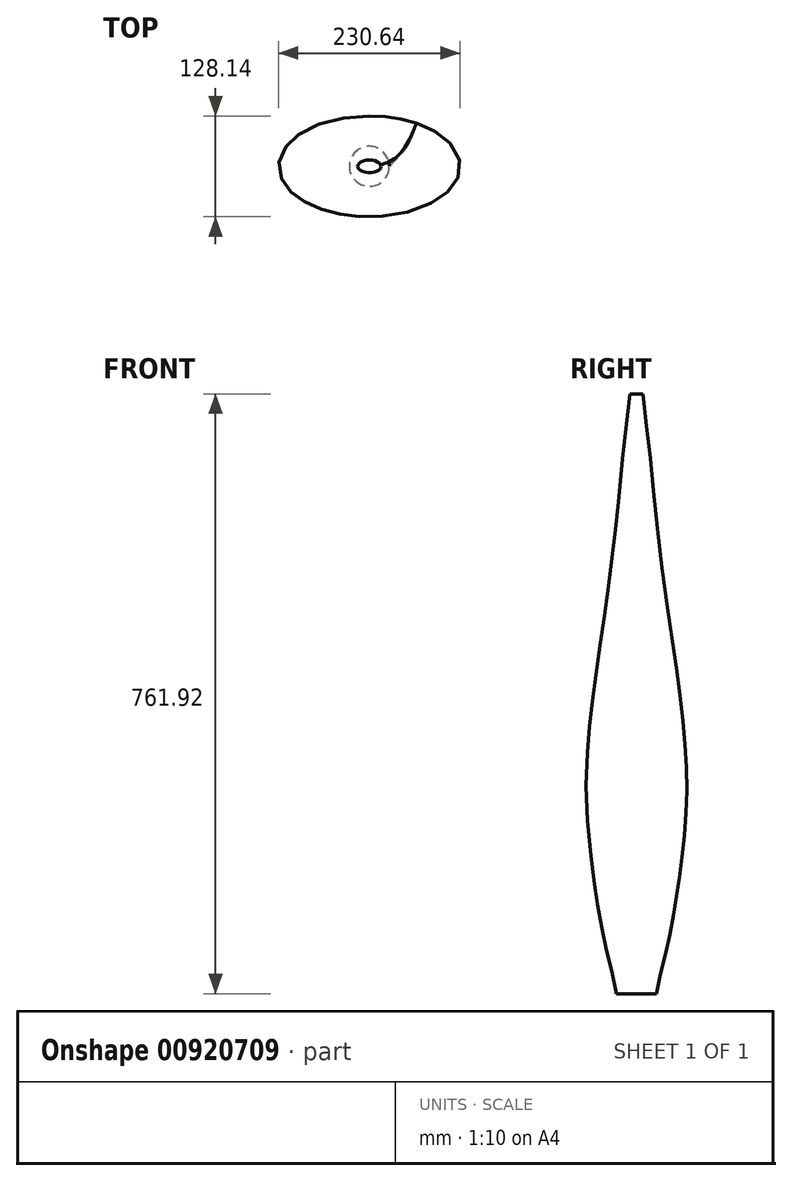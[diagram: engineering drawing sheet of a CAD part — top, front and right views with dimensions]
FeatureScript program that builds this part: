
annotation { "Feature Type Name" : "Feature", "Feature Type Description" : "" }
export const myFeature = defineFeature(function(context is Context, id is Id, definition is map)
    precondition{}
    {
        {
            var Q0;
            Q0=qCreatedBy(makeId("Top.planeOp"),FACE);
            var sketch = newSketch(context, id + "F0", { "sketchPlane" : qUnion([Q0])});
            skEllipse(sketch, "E0", {"center": v(0, 0) * mm, "majorRadius": 25.4 * mm, "minorRadius": 25.4 * mm, "majorAxis": v(1, 0)});
            skSolve(sketch);
        }
        {
            var Q0;
            Q0=qCreatedBy(makeId("Front.planeOp"),FACE);
            var sketch = newSketch(context, id + "F1", { "sketchPlane" : qUnion([Q0])});
            skLineSegment(sketch, "E1", {"start": v(0, 0) * mm, "end": v(0, 84.66) * mm, "construction": true});
            skPoint(sketch, "E2", {"position": v(0, 84.66) * mm});
            skPoint(sketch, "E3.0.1.0", {"position": v(0, 169.32) * mm});
            skPoint(sketch, "E3.0.2.0", {"position": v(0, 253.97) * mm});
            skPoint(sketch, "E3.0.3.0", {"position": v(0, 338.63) * mm});
            skPoint(sketch, "E3.0.4.0", {"position": v(0, 423.3) * mm});
            skPoint(sketch, "E3.0.5.0", {"position": v(0, 507.95) * mm});
            skPoint(sketch, "E3.0.6.0", {"position": v(0, 592.6) * mm});
            skPoint(sketch, "E3.0.7.0", {"position": v(0, 677.27) * mm});
            skPoint(sketch, "E3.0.8.0", {"position": v(0, 761.92) * mm});
            skLineSegment(sketch, "E3.direction1", {"start": v(0, 84.66) * mm, "end": v(25.4, 84.66) * mm, "construction": true});
            skLineSegment(sketch, "E3.direction2", {"start": v(0, 84.66) * mm, "end": v(0, 169.32) * mm, "construction": true});
            skSolve(sketch);
        }
        {
            var Q0;
            Q0=qCreatedBy(makeId("Top.planeOp"),FACE);
            var Q1;
            Q1=sQuery(id+"F1.wireOp",VERTEX,"E2");
            cPlane(context, id + "F2", {"entities" : qUnion([Q0, Q1]), "cplaneType" : CPlaneType.PLANE_POINT, "offset" : 25.4 * mm, "width" : 152.4 * mm, "height" : 152.4 * mm});
        }
        {
            var Q0;
            Q0=qCreatedBy(makeId("Top.planeOp"),FACE);
            var Q1;
            Q1=sQuery(id+"F1.wireOp",VERTEX,"E3.0.1.0");
            cPlane(context, id + "F3", {"entities" : qUnion([Q0, Q1]), "cplaneType" : CPlaneType.PLANE_POINT, "offset" : 25.4 * mm, "width" : 152.4 * mm, "height" : 152.4 * mm});
        }
        {
            var Q0;
            Q0=qCreatedBy(makeId("Top.planeOp"),FACE);
            var Q1;
            Q1=sQuery(id+"F1.wireOp",VERTEX,"E3.0.2.0");
            cPlane(context, id + "F4", {"entities" : qUnion([Q0, Q1]), "cplaneType" : CPlaneType.PLANE_POINT, "offset" : 25.4 * mm, "width" : 152.4 * mm, "height" : 152.4 * mm});
        }
        {
            var Q0;
            Q0=qCreatedBy(makeId("Top.planeOp"),FACE);
            var Q1;
            Q1=sQuery(id+"F1.wireOp",VERTEX,"E3.0.3.0");
            cPlane(context, id + "F5", {"entities" : qUnion([Q0, Q1]), "cplaneType" : CPlaneType.PLANE_POINT, "offset" : 25.4 * mm, "width" : 152.4 * mm, "height" : 152.4 * mm});
        }
        {
            var Q0;
            Q0=qCreatedBy(makeId("Top.planeOp"),FACE);
            var Q1;
            Q1=sQuery(id+"F1.wireOp",VERTEX,"E3.0.4.0");
            cPlane(context, id + "F6", {"entities" : qUnion([Q0, Q1]), "cplaneType" : CPlaneType.PLANE_POINT, "offset" : 25.4 * mm, "width" : 152.4 * mm, "height" : 152.4 * mm});
        }
        {
            var Q0;
            Q0=qCreatedBy(makeId("Top.planeOp"),FACE);
            var Q1;
            Q1=sQuery(id+"F1.wireOp",VERTEX,"E3.0.5.0");
            cPlane(context, id + "F7", {"entities" : qUnion([Q0, Q1]), "cplaneType" : CPlaneType.PLANE_POINT, "offset" : 25.4 * mm, "width" : 152.4 * mm, "height" : 152.4 * mm});
        }
        {
            var Q0;
            Q0=qCreatedBy(makeId("Top.planeOp"),FACE);
            var Q1;
            Q1=sQuery(id+"F1.wireOp",VERTEX,"E3.0.6.0");
            cPlane(context, id + "F8", {"entities" : qUnion([Q0, Q1]), "cplaneType" : CPlaneType.PLANE_POINT, "offset" : 25.4 * mm, "width" : 152.4 * mm, "height" : 152.4 * mm});
        }
        {
            var Q0;
            Q0=qCreatedBy(makeId("Top.planeOp"),FACE);
            var Q1;
            Q1=sQuery(id+"F1.wireOp",VERTEX,"E3.0.7.0");
            cPlane(context, id + "F9", {"entities" : qUnion([Q0, Q1]), "cplaneType" : CPlaneType.PLANE_POINT, "offset" : 25.4 * mm, "width" : 152.4 * mm, "height" : 152.4 * mm});
        }
        {
            var Q0;
            Q0=qCreatedBy(makeId("Top.planeOp"),FACE);
            var Q1;
            Q1=sQuery(id+"F1.wireOp",VERTEX,"E3.0.8.0");
            cPlane(context, id + "F10", {"entities" : qUnion([Q0, Q1]), "cplaneType" : CPlaneType.PLANE_POINT, "offset" : 25.4 * mm, "width" : 152.4 * mm, "height" : 152.4 * mm});
        }
        {
            var Q0;
            Q0=qCreatedBy(id+"F2.planeOp",FACE);
            var sketch = newSketch(context, id + "F11", { "sketchPlane" : qUnion([Q0])});
            skEllipse(sketch, "E4", {"center": v(0, 0) * mm, "majorRadius": 63.5 * mm, "minorRadius": 44.45 * mm, "majorAxis": v(1, 0)});
            skSolve(sketch);
        }
        {
            var Q0;
            Q0=qCreatedBy(id+"F3.planeOp",FACE);
            var sketch = newSketch(context, id + "F12", { "sketchPlane" : qUnion([Q0])});
            skEllipse(sketch, "E5", {"center": v(0, 0) * mm, "majorRadius": 102.74 * mm, "minorRadius": 57.15 * mm, "majorAxis": v(1, 0)});
            skSolve(sketch);
        }
        {
            var Q0;
            Q0=qCreatedBy(id+"F4.planeOp",FACE);
            var sketch = newSketch(context, id + "F13", { "sketchPlane" : qUnion([Q0])});
            skEllipse(sketch, "E6", {"center": v(0, 0) * mm, "majorRadius": 115.32 * mm, "minorRadius": 64 * mm, "majorAxis": v(1, 0)});
            skSolve(sketch);
        }
        {
            var Q0;
            Q0=qCreatedBy(id+"F5.planeOp",FACE);
            var sketch = newSketch(context, id + "F14", { "sketchPlane" : qUnion([Q0])});
            skEllipse(sketch, "E7", {"center": v(0, 0) * mm, "majorRadius": 107.44 * mm, "minorRadius": 59.7 * mm, "majorAxis": v(1, 0)});
            skSolve(sketch);
        }
        {
            var Q0;
            Q0=qCreatedBy(id+"F6.planeOp",FACE);
            var sketch = newSketch(context, id + "F15", { "sketchPlane" : qUnion([Q0])});
            skEllipse(sketch, "E8", {"center": v(0, 0) * mm, "majorRadius": 88.52 * mm, "minorRadius": 49.15 * mm, "majorAxis": v(1, 0)});
            skSolve(sketch);
        }
        {
            var Q0;
            Q0=qCreatedBy(id+"F7.planeOp",FACE);
            var sketch = newSketch(context, id + "F16", { "sketchPlane" : qUnion([Q0])});
            skEllipse(sketch, "E9", {"center": v(0, 0) * mm, "majorRadius": 66.3 * mm, "minorRadius": 36.83 * mm, "majorAxis": v(1, 0)});
            skSolve(sketch);
        }
        {
            var Q0;
            Q0=qCreatedBy(id+"F8.planeOp",FACE);
            var sketch = newSketch(context, id + "F17", { "sketchPlane" : qUnion([Q0])});
            skEllipse(sketch, "E10", {"center": v(0, 0) * mm, "majorRadius": 47.5 * mm, "minorRadius": 26.42 * mm, "majorAxis": v(1, 0)});
            skSolve(sketch);
        }
        {
            var Q0;
            Q0=qCreatedBy(id+"F9.planeOp",FACE);
            var sketch = newSketch(context, id + "F18", { "sketchPlane" : qUnion([Q0])});
            skEllipse(sketch, "E11", {"center": v(0, 0) * mm, "majorRadius": 31.75 * mm, "minorRadius": 17.78 * mm, "majorAxis": v(1, 0)});
            skSolve(sketch);
        }
        {
            var Q0;
            Q0=qCreatedBy(id+"F10.planeOp",FACE);
            var sketch = newSketch(context, id + "F19", { "sketchPlane" : qUnion([Q0])});
            skEllipse(sketch, "E12", {"center": v(0, 0) * mm, "majorRadius": 14.73 * mm, "minorRadius": 8.13 * mm, "majorAxis": v(1, 0)});
            skSolve(sketch);
        }
        {
            var Q0;
            Q0=makeQuery(id+"F0.imprint","IMPRINT",FACE,{"disambiguationData":[TD([[makeQuery(id+"F0.imprint","IMPRINT",EDGE,{"derivedFrom":sQuery(id+"F0.wireOp",EDGE,"E0")}),1.0]])]});
            var Q1;
            Q1=makeQuery(id+"F11.imprint","IMPRINT",FACE,{"disambiguationData":[TD([[makeQuery(id+"F11.imprint","IMPRINT",EDGE,{"derivedFrom":sQuery(id+"F11.wireOp",EDGE,"E4")}),1.0]])]});
            var Q2;
            Q2=makeQuery(id+"F12.imprint","IMPRINT",FACE,{"disambiguationData":[TD([[makeQuery(id+"F12.imprint","IMPRINT",EDGE,{"derivedFrom":sQuery(id+"F12.wireOp",EDGE,"E5")}),1.0]])]});
            var Q3;
            Q3=makeQuery(id+"F13.imprint","IMPRINT",FACE,{"disambiguationData":[TD([[makeQuery(id+"F13.imprint","IMPRINT",EDGE,{"derivedFrom":sQuery(id+"F13.wireOp",EDGE,"E6")}),1.0]])]});
            var Q4;
            Q4=makeQuery(id+"F14.imprint","IMPRINT",FACE,{"disambiguationData":[TD([[makeQuery(id+"F14.imprint","IMPRINT",EDGE,{"derivedFrom":sQuery(id+"F14.wireOp",EDGE,"E7")}),1.0]])]});
            var Q5;
            Q5=makeQuery(id+"F15.imprint","IMPRINT",FACE,{"disambiguationData":[TD([[makeQuery(id+"F15.imprint","IMPRINT",EDGE,{"derivedFrom":sQuery(id+"F15.wireOp",EDGE,"E8")}),1.0]])]});
            var Q6;
            Q6=makeQuery(id+"F16.imprint","IMPRINT",FACE,{"disambiguationData":[TD([[makeQuery(id+"F16.imprint","IMPRINT",EDGE,{"derivedFrom":sQuery(id+"F16.wireOp",EDGE,"E9")}),1.0]])]});
            var Q7;
            Q7=makeQuery(id+"F17.imprint","IMPRINT",FACE,{"disambiguationData":[TD([[makeQuery(id+"F17.imprint","IMPRINT",EDGE,{"derivedFrom":sQuery(id+"F17.wireOp",EDGE,"E10")}),1.0]])]});
            var Q8;
            Q8=makeQuery(id+"F18.imprint","IMPRINT",FACE,{"disambiguationData":[TD([[makeQuery(id+"F18.imprint","IMPRINT",EDGE,{"derivedFrom":sQuery(id+"F18.wireOp",EDGE,"E11")}),1.0]])]});
            var Q9;
            Q9=makeQuery(id+"F19.imprint","IMPRINT",FACE,{"disambiguationData":[TD([[makeQuery(id+"F19.imprint","IMPRINT",EDGE,{"derivedFrom":sQuery(id+"F19.wireOp",EDGE,"E12")}),1.0]])]});
            loft(context, id + "F20", {"sheetProfilesArray" : [{ "sheetProfileEntities" : qUnion([Q0]) }, { "sheetProfileEntities" : qUnion([Q1]) }, { "sheetProfileEntities" : qUnion([Q2]) }, { "sheetProfileEntities" : qUnion([Q3]) }, { "sheetProfileEntities" : qUnion([Q4]) }, { "sheetProfileEntities" : qUnion([Q5]) }, { "sheetProfileEntities" : qUnion([Q6]) }, { "sheetProfileEntities" : qUnion([Q7]) }, { "sheetProfileEntities" : qUnion([Q8]) }, { "sheetProfileEntities" : qUnion([Q9]) }]});
        }
    });
